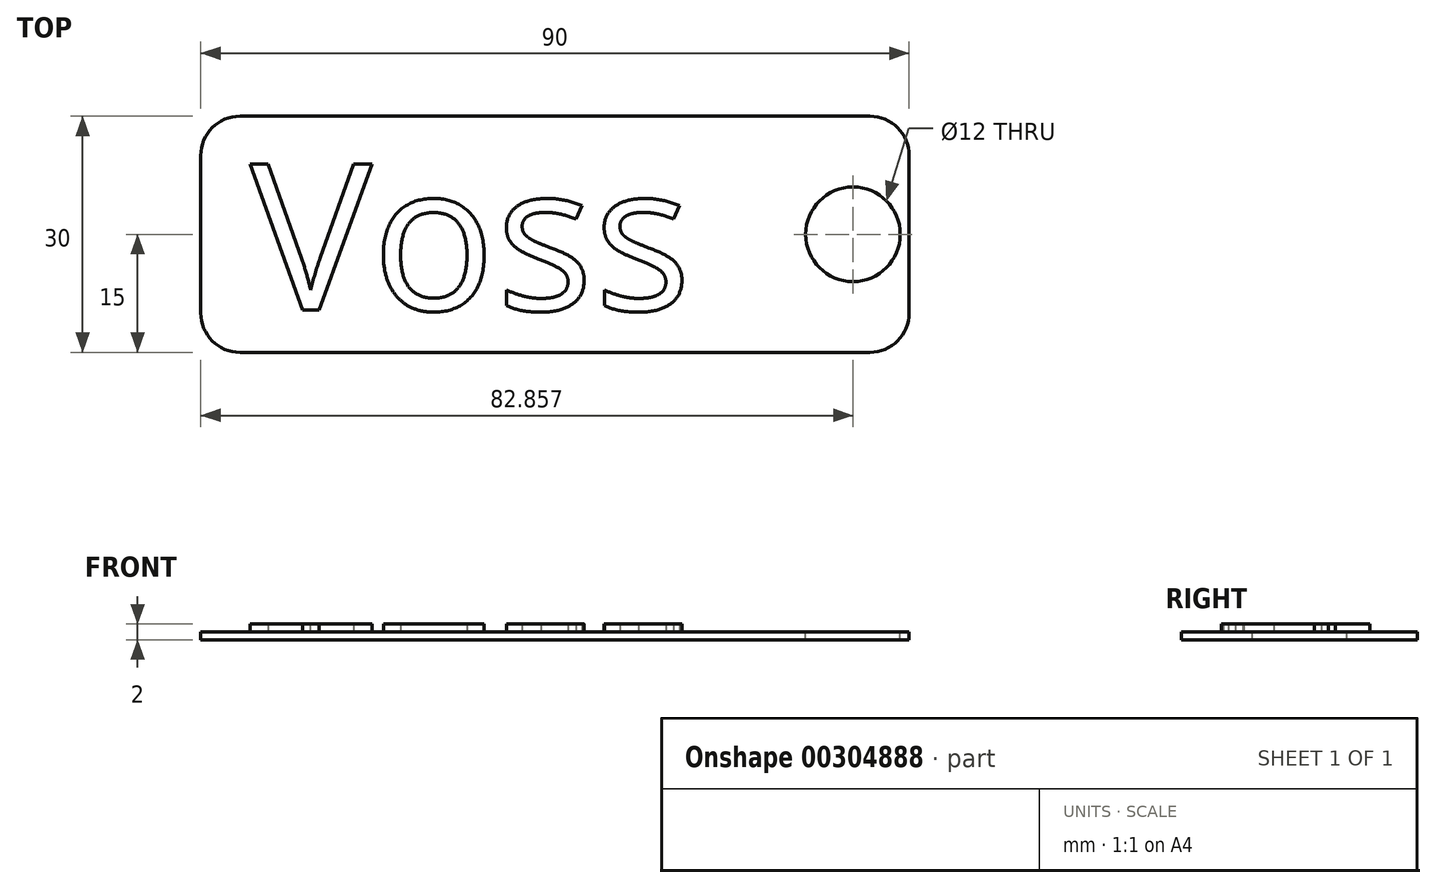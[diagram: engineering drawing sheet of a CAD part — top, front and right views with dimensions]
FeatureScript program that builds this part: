
annotation { "Feature Type Name" : "Feature", "Feature Type Description" : "" }
export const myFeature = defineFeature(function(context is Context, id is Id, definition is map)
    precondition{}
    {
        {
            var Q0;
            Q0=qCreatedBy(makeId("Top.planeOp"),FACE);
            var sketch = newSketch(context, id + "F0", { "sketchPlane" : qUnion([Q0])});
            skLineSegment(sketch, "E0.bottom", {"start": v(-45, -15) * mm, "end": v(45, -15) * mm});
            skLineSegment(sketch, "E0.top", {"start": v(-45, 15) * mm, "end": v(45, 15) * mm});
            skLineSegment(sketch, "E0.left", {"start": v(-45, -15) * mm, "end": v(-45, 15) * mm});
            skLineSegment(sketch, "E0.right", {"start": v(45, -15) * mm, "end": v(45, 15) * mm});
            skPoint(sketch, "E0.middle", {"position": v(0, 0) * mm});
            skSolve(sketch);
        }
        {
            var Q0;
            Q0 = qSketchRegion(id + "F0", true);
            extrude(context, id + "F1", {"entities" : qUnion([Q0]), "depth" : 1 * mm});
        }
        {
            var Q0;
            Q0=makeQuery(id+"F1.opExtrude","SWEPT_EDGE",EDGE,{"disambiguationData":[OSD([sQuery(id+"F0.wireOp",EDGE,"E0.bottom"),sQuery(id+"F0.wireOp",EDGE,"E0.left")])]});
            var Q1;
            Q1=makeQuery(id+"F1.opExtrude","SWEPT_EDGE",EDGE,{"disambiguationData":[OSD([sQuery(id+"F0.wireOp",EDGE,"E0.bottom"),sQuery(id+"F0.wireOp",EDGE,"E0.right")])]});
            var Q2;
            Q2=makeQuery(id+"F1.opExtrude","SWEPT_EDGE",EDGE,{"disambiguationData":[OSD([sQuery(id+"F0.wireOp",EDGE,"E0.top"),sQuery(id+"F0.wireOp",EDGE,"E0.right")])]});
            var Q3;
            Q3=makeQuery(id+"F1.opExtrude","SWEPT_EDGE",EDGE,{"disambiguationData":[OSD([sQuery(id+"F0.wireOp",EDGE,"E0.top"),sQuery(id+"F0.wireOp",EDGE,"E0.left")])]});
            fillet(context, id + "F2", {"entities" : qUnion([Q0, Q1, Q2, Q3]), "radius" : 5 * mm, "tangentPropagation" : true, "allowEdgeOverflow" : false});
        }
        {
            var Q0;
            Q0=makeQuery(id+"F1.opExtrude","CAP_FACE",FACE,{"disambiguationData":[OSD([sQuery(id+"F0.wireOp",EDGE,"E0.bottom"),sQuery(id+"F0.wireOp",EDGE,"E0.top"),sQuery(id+"F0.wireOp",EDGE,"E0.left"),sQuery(id+"F0.wireOp",EDGE,"E0.right")])],"isStart":false});
            var sketch = newSketch(context, id + "F3", { "sketchPlane" : qUnion([Q0])});
            skText(sketch, "E1", { "text": "Voss", "fontName": "OpenSans-Regular.ttf"});
            const initialGuessF3  = {"E1": [-0.03875, -0.00964, 1, 0, 0.01875]};
            skSetInitialGuess(sketch, initialGuessF3);
            skSolve(sketch);
        }
        {
            var Q0;
            Q0 = qSketchRegion(id + "F3", true);
            extrude(context, id + "F4", {"entities" : qUnion([Q0]), "operationType" : NewBodyOperationType.ADD, "depth" : 1 * mm});
        }
        {
            var Q0;
            {var subQ0=sQuery(id+"F0.wireOp",EDGE,"E0.right");var subQ1=sQuery(id+"F0.wireOp",EDGE,"E0.top");var subQ2=sQuery(id+"F0.wireOp",EDGE,"E0.left");var subQ3=sQuery(id+"F0.wireOp",EDGE,"E0.bottom");Q0=makeQuery(id+"F4.boolean.opBoolean","SPLIT",FACE,{"disambiguationData":[TD([makeQuery(id+"F1.opExtrude","SWEPT_FACE",FACE,{"disambiguationData":[OSD([subQ3])]})])],"derivedFrom":makeQuery(id+"F1.opExtrude","CAP_FACE",FACE,{"disambiguationData":[OSD([subQ3,subQ1,subQ2,subQ0])],"isStart":false})});}
            var sketch = newSketch(context, id + "F5", { "sketchPlane" : qUnion([Q0])});
            skPoint(sketch, "E2", {"position": v(37.86, 0) * mm});
            skSolve(sketch);
        }
        {
            var Q0;
            Q0=sQuery(id+"F5.wireOp",VERTEX,"E2");
            var Q1;
            Q1=makeQuery(id+"F1.opExtrude","SWEPT_BODY",BODY,{"disambiguationData":[OSD([sQuery(id+"F0.wireOp",EDGE,"E0.bottom"),sQuery(id+"F0.wireOp",EDGE,"E0.top"),sQuery(id+"F0.wireOp",EDGE,"E0.left"),sQuery(id+"F0.wireOp",EDGE,"E0.right")])]});
            hole(context, id + "F6", {"style" : HoleStyle.SIMPLE, "endStyle" : HoleEndStyle.BLIND, "holeDiameter" : 12 * mm, "holeDepth" : 15.5 * mm, "tappedDepth" : 12 * mm, "tapClearance" : 3, "locations" : qUnion([Q0]), "scope" : qUnion([Q1])});
        }
    });
